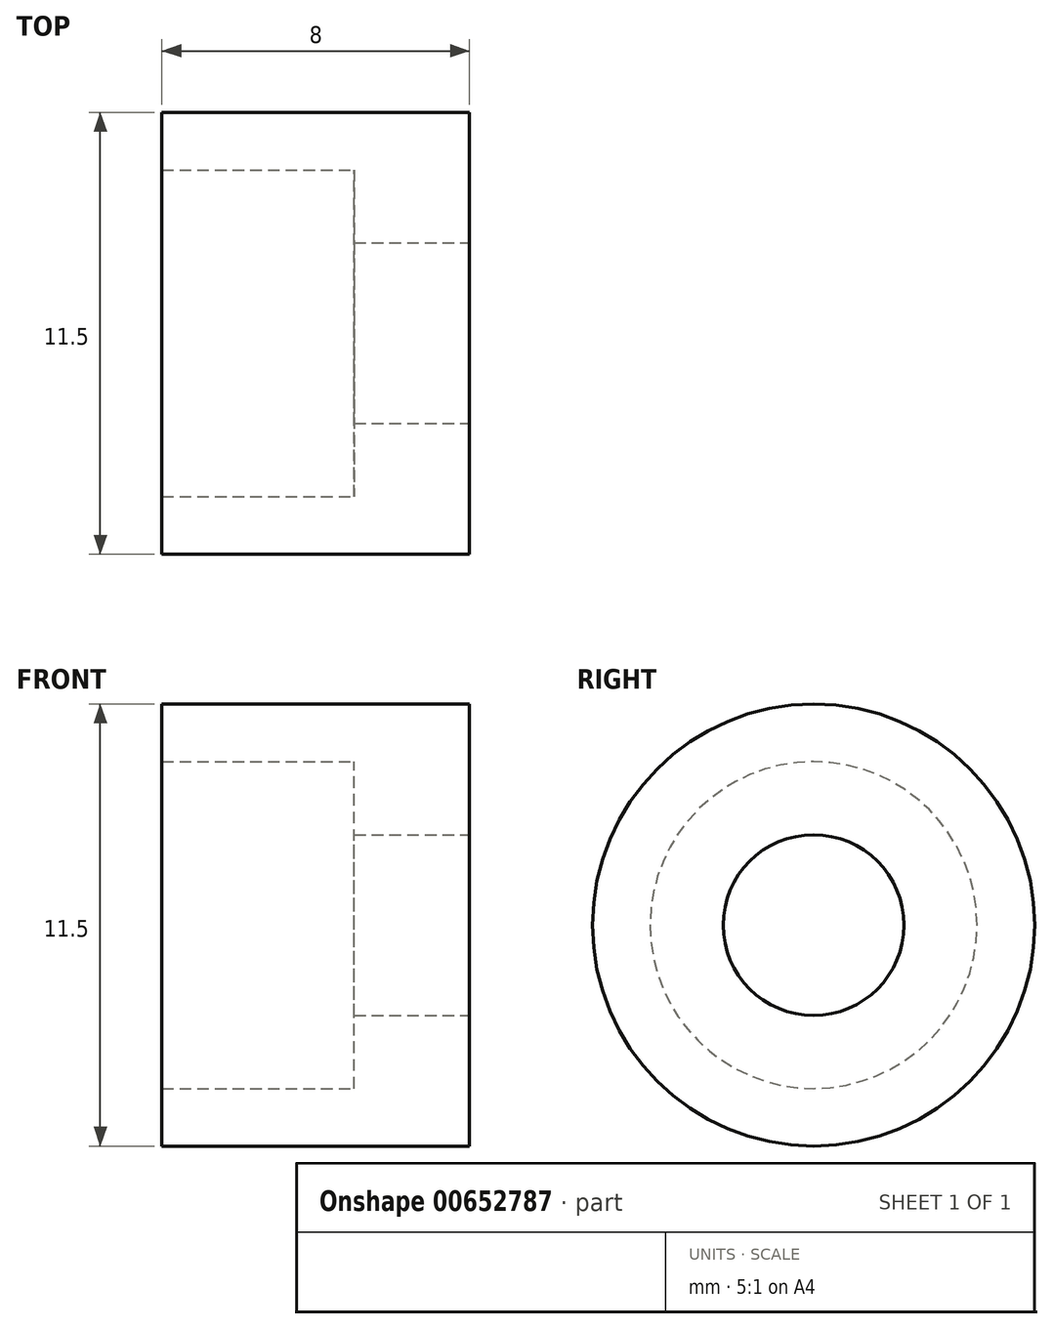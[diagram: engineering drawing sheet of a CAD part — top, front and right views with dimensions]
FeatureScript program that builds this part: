
annotation { "Feature Type Name" : "Feature", "Feature Type Description" : "" }
export const myFeature = defineFeature(function(context is Context, id is Id, definition is map)
    precondition{}
    {
        {
            var Q0;
            Q0=qCreatedBy(makeId("Front.planeOp"),FACE);
            var sketch = newSketch(context, id + "F0", { "sketchPlane" : qUnion([Q0])});
            skLineSegment(sketch, "E0", {"start": v(0, 0) * mm, "end": v(0, 5.75) * mm});
            skLineSegment(sketch, "E1", {"start": v(0, 5.75) * mm, "end": v(8, 5.75) * mm});
            skLineSegment(sketch, "E2", {"start": v(8, 5.75) * mm, "end": v(8, 0) * mm});
            skLineSegment(sketch, "E3", {"start": v(8, 0) * mm, "end": v(0, 0) * mm});
            skLineSegment(sketch, "E4", {"start": v(0, 4.25) * mm, "end": v(5, 4.25) * mm});
            skLineSegment(sketch, "E5", {"start": v(5, 4.25) * mm, "end": v(5, 2.35) * mm});
            skLineSegment(sketch, "E6", {"start": v(5, 2.35) * mm, "end": v(8, 2.35) * mm});
            skSolve(sketch);
        }
        {
            var Q0;
            {var subQ1=sQuery(id+"F0.wireOp",EDGE,"E1");Q0=makeQuery(id+"F0.imprint","IMPRINT",FACE,{"disambiguationData":[TD([[makeQuery(id+"F0.imprint","IMPRINT",EDGE,{"derivedFrom":subQ1}),-1.0]])]});}
            var Q1;
            Q1=sQuery(id+"F0.wireOp",EDGE,"E3");
            revolve(context, id + "F1", {"entities" : qUnion([Q0]), "axis" : qUnion([Q1]), "revolveType" : RevolveType.FULL});
        }
    });
